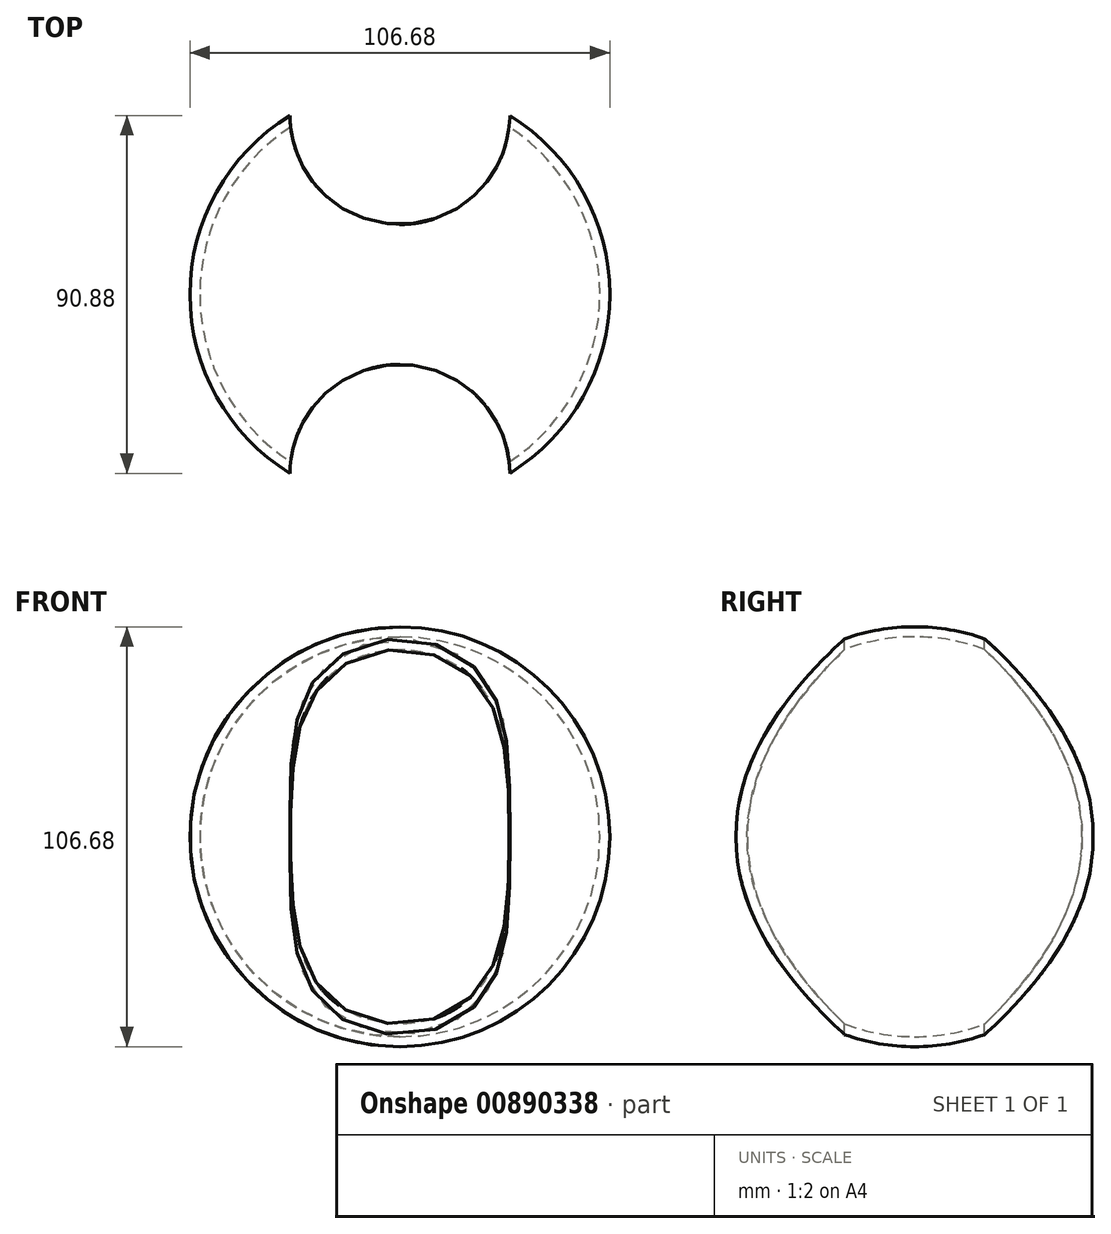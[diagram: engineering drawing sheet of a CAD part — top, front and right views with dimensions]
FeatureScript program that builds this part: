
annotation { "Feature Type Name" : "Feature", "Feature Type Description" : "" }
export const myFeature = defineFeature(function(context is Context, id is Id, definition is map)
    precondition{}
    {
        {
            var Q0;
            Q0=qCreatedBy(makeId("Front.planeOp"),FACE);
            var sketch = newSketch(context, id + "F0", { "sketchPlane" : qUnion([Q0])});
            skCircle(sketch, "E0", {"center": v(0, 0) * mm, "radius": 50.8 * mm});
            skCircle(sketch, "E1.0", {"center": v(0, 0) * mm, "radius": 53.34 * mm});
            skLineSegment(sketch, "E2", {"start": v(0, 68.73) * mm, "end": v(0, -73.44) * mm});
            skSolve(sketch);
        }
        {
            var Q0;
            {var subQ0=sQuery(id+"F0.wireOp",EDGE,"E2");var subQ1=sQuery(id+"F0.wireOp",EDGE,"E0");var subQ2=makeQuery(id+"F0.imprint","INTERSECT",VERTEX,{"disambiguationData":[OD(0.0)],"derivedFrom":[subQ1,subQ0]});Q0=makeQuery(id+"F0.imprint","IMPRINT",FACE,{"disambiguationData":[TD([[makeQuery(id+"F0.imprint","IMPRINT",EDGE,{"disambiguationData":[TD([[subQ2,-1.0]])],"derivedFrom":subQ1}),-1.0]])]});}
            var Q1;
            Q1=sQuery(id+"F0.wireOp",EDGE,"E1.0");
            var Q2;
            Q2=sQuery(id+"F0.wireOp",EDGE,"E0");
            var Q3;
            Q3=sQuery(id+"F0.wireOp",EDGE,"E2");
            revolve(context, id + "F1", {"surfaceOperationType" : NewSurfaceOperationType.NEW, "entities" : qUnion([Q0]), "surfaceEntities" : qUnion([Q1, Q2]), "axis" : qUnion([Q3]), "revolveType" : RevolveType.ONE_DIRECTION, "angle" : 360 * degree});
        }
        {
            var Q0;
            Q0=qCreatedBy(makeId("Top.planeOp"),FACE);
            var sketch = newSketch(context, id + "F2", { "sketchPlane" : qUnion([Q0])});
            skCircle(sketch, "E3", {"center": v(0, 45.72) * mm, "radius": 27.94 * mm});
            skCircle(sketch, "E4", {"center": v(0, -45.72) * mm, "radius": 27.94 * mm});
            skSolve(sketch);
        }
        {
            var Q0;
            Q0=makeQuery(id+"F2.imprint","IMPRINT",FACE,{"disambiguationData":[TD([[makeQuery(id+"F2.imprint","IMPRINT",EDGE,{"derivedFrom":sQuery(id+"F2.wireOp",EDGE,"E3")}),1.0]])]});
            var Q1;
            Q1=makeQuery(id+"F2.imprint","IMPRINT",FACE,{"disambiguationData":[TD([[makeQuery(id+"F2.imprint","IMPRINT",EDGE,{"derivedFrom":sQuery(id+"F2.wireOp",EDGE,"E4")}),1.0]])]});
            var Q2;
            Q2=sQuery(id+"F2.wireOp",EDGE,"E3");
            extrude(context, id + "F3", {"entities" : qUnion([Q0, Q1]), "operationType" : NewBodyOperationType.REMOVE, "surfaceEntities" : qUnion([Q2]), "endBound" : BoundingType.SYMMETRIC, "oppositeDirection" : true, "depth" : 127 * mm, "offsetDistance" : 25.4 * mm});
        }
        {
            var Q0;
            Q0=qCreatedBy(makeId("Top.planeOp"),FACE);
            var sketch = newSketch(context, id + "F4", { "sketchPlane" : qUnion([Q0])});
            skLineSegment(sketch, "E5", {"start": v(29.4, -62.26) * mm, "end": v(-43.5, 0) * mm});
            skLineSegment(sketch, "E6", {"start": v(-43.5, 0) * mm, "end": v(14.23, 43.7) * mm});
            skLineSegment(sketch, "E7", {"start": v(14.23, 43.7) * mm, "end": v(47.3, 0) * mm});
            skLineSegment(sketch, "E8", {"start": v(47.3, 0) * mm, "end": v(29.4, -62.26) * mm});
            skSolve(sketch);
        }
        {
            var Q0;
            Q0=sQuery(id+"F4.wireOp",EDGE,"E5");
            var Q1;
            Q1=sQuery(id+"F4.wireOp",EDGE,"E8");
            var Q2;
            Q2=sQuery(id+"F4.wireOp",EDGE,"E7");
            var Q3;
            Q3=sQuery(id+"F4.wireOp",EDGE,"E6");
            extrude(context, id + "F5", {"bodyType" : ToolBodyType.SURFACE, "surfaceEntities" : qUnion([Q0, Q1, Q2, Q3]), "depth" : 138.94 * mm, "offsetDistance" : 25.4 * mm});
        }
    });
